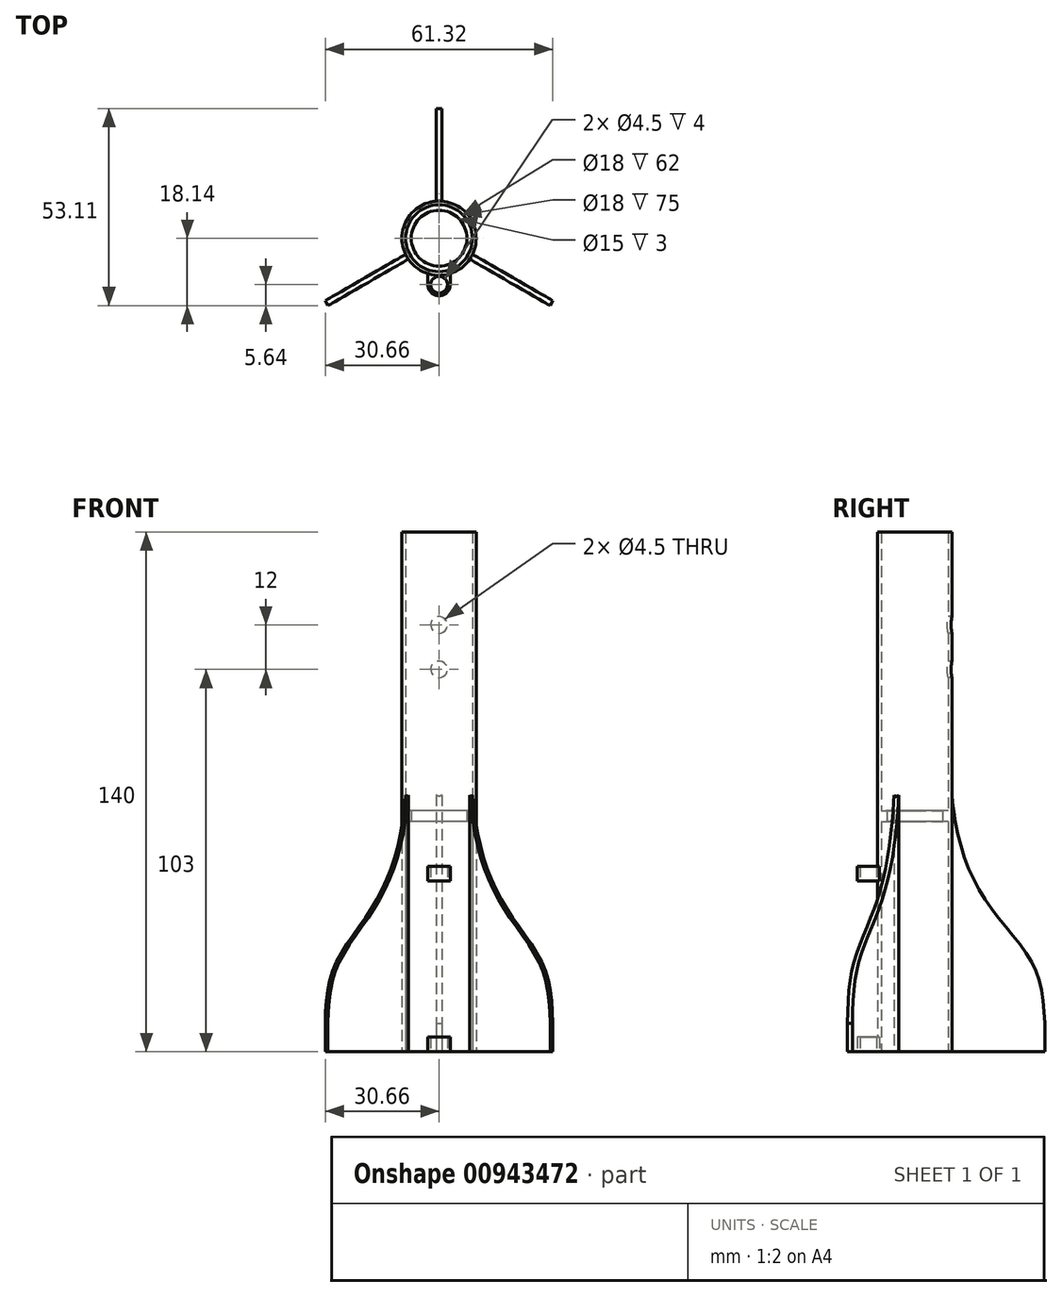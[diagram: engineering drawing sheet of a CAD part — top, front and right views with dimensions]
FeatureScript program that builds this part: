
annotation { "Feature Type Name" : "Feature", "Feature Type Description" : "" }
export const myFeature = defineFeature(function(context is Context, id is Id, definition is map)
    precondition{}
    {
        {
            var Q0;
            Q0=qCreatedBy(makeId("Top.planeOp"),FACE);
            var sketch = newSketch(context, id + "F0", { "sketchPlane" : qUnion([Q0])});
            skCircle(sketch, "E0", {"center": v(0, 0) * mm, "radius": 9 * mm});
            skCircle(sketch, "E1", {"center": v(0, -12.5) * mm, "radius": 2.25 * mm});
            skArc(sketch, "E2", {"start": v(-1.48, -9.89) * mm, "mid": v(0, -15.5) * mm, "end": v(1.48, -9.9) * mm});
            skLineSegment(sketch, "E3", {"start": v(3, -12.5) * mm, "end": v(3, -9.54) * mm});
            skLineSegment(sketch, "E4", {"start": v(-3, -12.5) * mm, "end": v(-3, -9.54) * mm});
            skLineSegment(sketch, "E5.top", {"start": v(0.75, 34.97) * mm, "end": v(-0.75, 34.97) * mm});
            skLineSegment(sketch, "E5.left", {"start": v(0.75, 9.97) * mm, "end": v(0.75, 34.97) * mm});
            skLineSegment(sketch, "E5.right", {"start": v(-0.75, 9.97) * mm, "end": v(-0.75, 34.97) * mm});
            skPoint(sketch, "E5.middle", {"position": v(0, 22.47) * mm});
            skCircle(sketch, "E6", {"center": v(0, 0) * mm, "radius": 10 * mm});
            skCircle(sketch, "E7", {"center": v(0, 0) * mm, "radius": 7.5 * mm});
            skSolve(sketch);
        }
        {
            var Q0;
            Q0=makeQuery(id+"F0.imprint","IMPRINT",FACE,{"disambiguationData":[TD([[makeQuery(id+"F0.imprint","IMPRINT",EDGE,{"derivedFrom":sQuery(id+"F0.wireOp",EDGE,"E0")}),-1.0]])]});
            var Q1;
            {var subQ0=sQuery(id+"F0.wireOp",EDGE,"ZZ5YX0io-akKa-NGHC-uEbq-0SfljBpc04vF");Q1=makeQuery(id+"F0.imprint","IMPRINT",FACE,{"disambiguationData":[TD([[makeQuery(id+"F0.imprint","IMPRINT",EDGE,{"derivedFrom":subQ0}),1.0]])]});}
            extrude(context, id + "F1", {"entities" : qUnion([Q0, Q1]), "depth" : 140 * mm, "offsetDistance" : 25 * mm});
        }
        {
            var Q0;
            Q0=makeQuery(id+"F0.imprint","IMPRINT",FACE,{"disambiguationData":[TD([[makeQuery(id+"F0.imprint","IMPRINT",EDGE,{"derivedFrom":sQuery(id+"F0.wireOp",EDGE,"E5.top")}),1.0]])]});
            extrude(context, id + "F2", {"entities" : qUnion([Q0]), "operationType" : NewBodyOperationType.ADD, "depth" : 100 * mm, "offsetDistance" : 25 * mm});
        }
        {
            var Q0;
            Q0=makeQuery(id+"F2.opExtrude","SWEPT_FACE",FACE,{"disambiguationData":[OSD([sQuery(id+"F0.wireOp",EDGE,"E5.left")])]});
            var sketch = newSketch(context, id + "F3", { "sketchPlane" : qUnion([Q0])});
            skFitSpline(sketch, "E8", {"points": [v(9.97, 75) * mm, v(9.97, 69.16) * mm, v(12.9, 53.8) * mm, v(21.82, 36.99) * mm, v(32.08, 23.03) * mm, v(34.97, 7.7) * mm, v(34.97, -12.88) * mm, v(34.97, -25) * mm], "startDerivative": vector(0, -120.5) * mm, "endDerivative": vector(0, -110.6) * mm});
            skPoint(sketch, "E9", {"position": v(35.08, 25) * mm});
            skSolve(sketch);
        }
        {
            var Q0;
            {var subQ1=sQuery(id+"F0.wireOp",EDGE,"E5.left");var subQ2=makeQuery(id+"F2.opExtrude","CAP_EDGE",EDGE,{"disambiguationData":[OSD([subQ1])],"isStart":false});Q0=makeQuery(id+"F3.imprint","IMPRINT",FACE,{"disambiguationData":[TD([[makeQuery(id+"F3.imprint","IMPRINT",EDGE,{"derivedFrom":subQ2}),-1.0]])]});}
            extrude(context, id + "F4", {"entities" : qUnion([Q0]), "operationType" : NewBodyOperationType.REMOVE, "endBound" : BoundingType.THROUGH_ALL, "oppositeDirection" : true, "depth" : 25 * mm, "offsetDistance" : 25 * mm});
        }
        {
            var Q0;
            Q0=makeQuery(id+"F1.opExtrude","SWEPT_BODY",BODY,{"disambiguationData":[OSD([sQuery(id+"F0.wireOp",EDGE,"E0"),sQuery(id+"F0.wireOp",EDGE,"lXoG40gP-U72Z-pVJZ-Nn51-esoHy9KuEW7K")])]});
            var Q1;
            Q1=sQuery(id+"F0.wireOp",EDGE,"E0");
            circularPattern(context, id + "F5", {"entities" : qUnion([Q0]), "axis" : qUnion([Q1]), "angle" : 360 * degree, "instanceCount" : 3, "equalSpace" : true, "isCentered" : true});
        }
        {
            var Q0;
            {var subQ0=sQuery(id+"F0.wireOp",EDGE,"E1");Q0=makeQuery(id+"F0.imprint","IMPRINT",FACE,{"disambiguationData":[TD([[makeQuery(id+"F0.imprint","IMPRINT",EDGE,{"derivedFrom":subQ0}),-1.0]])]});}
            var Q1;
            {var subQ3=sQuery(id+"F0.wireOp",EDGE,"E4");Q1=makeQuery(id+"F0.imprint","IMPRINT",FACE,{"disambiguationData":[TD([[makeQuery(id+"F0.imprint","IMPRINT",EDGE,{"derivedFrom":subQ3}),-1.0]])]});}
            var Q2;
            {var subQ3=sQuery(id+"F0.wireOp",EDGE,"E3");Q2=makeQuery(id+"F0.imprint","IMPRINT",FACE,{"disambiguationData":[TD([[makeQuery(id+"F0.imprint","IMPRINT",EDGE,{"derivedFrom":subQ3}),1.0]])]});}
            extrude(context, id + "F6", {"entities" : qUnion([Q0, Q1, Q2]), "operationType" : NewBodyOperationType.ADD, "depth" : 4 * mm, "offsetDistance" : 25 * mm});
        }
        {
            var Q0;
            Q0=makeQuery(id+"F0.imprint","IMPRINT",FACE,{"disambiguationData":[TD([[makeQuery(id+"F0.imprint","IMPRINT",EDGE,{"derivedFrom":sQuery(id+"F0.wireOp",EDGE,"E1")}),-1.0]])]});
            var Q1;
            {var subQ3=sQuery(id+"F0.wireOp",EDGE,"E4");Q1=makeQuery(id+"F0.imprint","IMPRINT",FACE,{"disambiguationData":[TD([[makeQuery(id+"F0.imprint","IMPRINT",EDGE,{"derivedFrom":subQ3}),-1.0]])]});}
            var Q2;
            {var subQ3=sQuery(id+"F0.wireOp",EDGE,"E3");Q2=makeQuery(id+"F0.imprint","IMPRINT",FACE,{"disambiguationData":[TD([[makeQuery(id+"F0.imprint","IMPRINT",EDGE,{"derivedFrom":subQ3}),1.0]])]});}
            extrude(context, id + "F7", {"entities" : qUnion([Q0, Q1, Q2]), "operationType" : NewBodyOperationType.ADD, "depth" : 50 * mm, "offsetDistance" : 25 * mm, "hasSecondDirection" : true, "secondDirectionOppositeDirection" : false, "secondDirectionDepth" : 46 * mm});
        }
        {
            var Q0;
            Q0=makeQuery(id+"F0.imprint","IMPRINT",FACE,{"disambiguationData":[TD([[makeQuery(id+"F0.imprint","IMPRINT",EDGE,{"derivedFrom":sQuery(id+"F0.wireOp",EDGE,"E0")}),1.0]])]});
            extrude(context, id + "F8", {"entities" : qUnion([Q0]), "operationType" : NewBodyOperationType.ADD, "depth" : 65 * mm, "offsetDistance" : 25 * mm, "hasSecondDirection" : true, "secondDirectionOppositeDirection" : false, "secondDirectionDepth" : 62 * mm});
        }
        {
            var Q0;
            Q0=qCreatedBy(makeId("Front.planeOp"),FACE);
            var sketch = newSketch(context, id + "F9", { "sketchPlane" : qUnion([Q0])});
            skLineSegment(sketch, "E10", {"start": v(0, 103) * mm, "end": v(0, 115) * mm});
            skLineSegment(sketch, "E11.0", {"start": v(-10, 140) * mm, "end": v(10, 140) * mm});
            skCircle(sketch, "E12", {"center": v(0, 115) * mm, "radius": 2.25 * mm});
            skCircle(sketch, "E13", {"center": v(0, 103) * mm, "radius": 2.25 * mm});
            skSolve(sketch);
        }
        {
            var Q0;
            Q0 = qSketchRegion(id + "F9", true);
            extrude(context, id + "F10", {"entities" : qUnion([Q0]), "operationType" : NewBodyOperationType.REMOVE, "oppositeDirection" : true, "depth" : 25 * mm, "offsetDistance" : 25 * mm});
        }
    });
